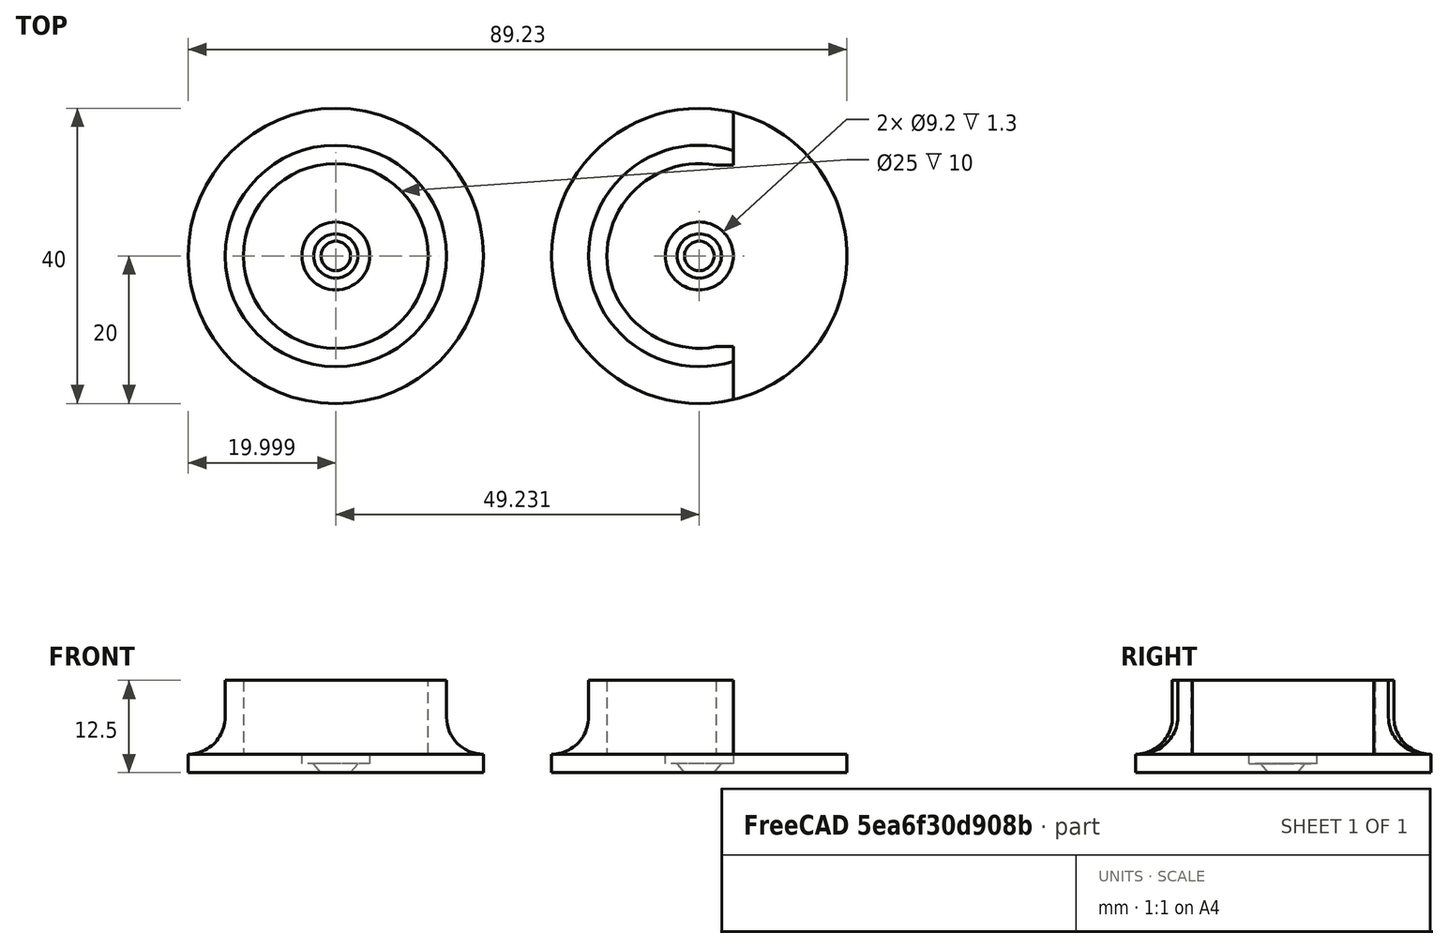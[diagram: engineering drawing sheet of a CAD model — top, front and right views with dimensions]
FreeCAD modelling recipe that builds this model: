
FCSTD DOCUMENT  (FreeCAD 0.20R29177 +233 (Git))
Label: FogasTarto
License: All rights reserved
LicenseURL: http://en.wikipedia.org/wiki/All_rights_reserved
objects: Part::Part2DObjectPython×10, Part::Cut×7, Part::Extrusion×5, Part::Cylinder×2, Part::MultiFuse×2, Part::Refine×2, Part::FeaturePython×1, Part::Torus×1, Part::Cone×1, Part::Feature×1
note: 32 computed .brp shape members not serialized (recipe doc carries the construction recipe); baked Part::Feature solids carry a one-line shape summary decoded from their .brp

FEATURE [Part::Cylinder] Cylinder
  Angle = 360
  AttacherType = Attacher::AttachEngine3D
  FirstAngle = 0
  Height = 10
  Radius = 12.5
  SecondAngle = 0
FEATURE [Part::Cylinder] Cylinder001
  Angle = 360
  AttacherType = Attacher::AttachEngine3D
  FirstAngle = 0
  Height = 10
  Radius = 15
  SecondAngle = 0
FEATURE [Part::Cut] Cut
  Base = -> Cylinder001
  Tool = -> Cylinder
FEATURE [Part::FeaturePython] Tube  # WARN: FeaturePython — macro-defined, semantics opaque (R4)
  AttacherType = Attacher::AttachEngine3D
  Height = 5
  InnerRadius = 15
  OuterRadius = 20
FEATURE [Part::Torus] Torus
  Angle1 = -180
  Angle2 = 180
  Angle3 = 360
  AttacherType = Attacher::AttachEngine3D
  Placement = pos=(0,-4.7e-15,5) rot=(0,0,1;0rad)
  Radius1 = 20
  Radius2 = 5
FEATURE [Part::Cut] Cut001
  Base = -> Tube
  Tool = -> Torus
FEATURE [Part::MultiFuse] Fusion
  Shapes = -> [Cut001,Cut]
FEATURE [Part::Part2DObjectPython] Circle  # Draft 2D object (typed FeaturePython)
  Area = 1256.64
  FirstAngle = 0
  LastAngle = 0
  MakeFace = true
  Placement = pos=(-7.1e-15,-3.7e-15,0) rot=(1,0,0;3.14159rad)
  Radius = 20
FEATURE [Part::Extrusion] Extrusion
  Base = -> Circle
  Dir = (0,0,-2.5)
  DirMode = 0
  FaceMakerClass = Part::FaceMakerBullseye
  LengthFwd = 0
  LengthRev = 0
  Solid = true
  Symmetric = false
FEATURE [Part::Part2DObjectPython] Circle001  # Draft 2D object (typed FeaturePython)
  Area = 12.5664
  FirstAngle = 0
  LastAngle = 0
  MakeFace = true
  Placement = pos=(-1.07e-14,-3e-15,-2.5) rot=(1,0,0;3.14159rad)
  Radius = 2
FEATURE [Part::Extrusion] Extrusion001
  Base = -> Circle001
  Dir = (0,0,42.0734)
  DirMode = 0
  FaceMakerClass = Part::FaceMakerBullseye
  LengthFwd = 0
  LengthRev = 0
  Solid = true
  Symmetric = false
FEATURE [Part::Cut] Cut002
  Base = -> Extrusion
  Tool = -> Extrusion001
FEATURE [Part::Part2DObjectPython] Circle002  # Draft 2D object (typed FeaturePython)
  Area = 66.4761
  FirstAngle = 0
  LastAngle = 0
  MakeFace = true
  Placement = pos=(-1.42e-14,-2.8e-15,0) rot=(0,0,1;0rad)
  Radius = 4.6
FEATURE [Part::Extrusion] Extrusion002
  Base = -> Circle002
  Dir = (0,0,-1.3)
  DirMode = 0
  FaceMakerClass = Part::FaceMakerBullseye
  LengthFwd = 0
  LengthRev = 0
  Solid = true
  Symmetric = false
FEATURE [Part::Cut] Cut003
  Base = -> Cut002
  Tool = -> Extrusion002
FEATURE [Part::Cone] Cone
  Angle = 360
  AttacherType = Attacher::AttachEngine3D
  Height = 1.2
  Placement = pos=(0,-3.1e-15,-2.5) rot=(0,0,1;0rad)
  Radius1 = 2
  Radius2 = 3
FEATURE [Part::Cut] Cut004
  Base = -> Cut003
  Tool = -> Cone
FEATURE [Part::MultiFuse] Fusion001
  Shapes = -> [Cut004,Fusion]
FEATURE [Part::Part2DObjectPython] Rectangle  # Draft 2D object (typed FeaturePython)
  Area = 3003.98
  ChamferSize = 0
  Columns = 1
  FilletRadius = 0
  Height = 50.7941
  Length = 59.1403
  MakeFace = true
  Placement = pos=(4.6,29.5702,3.6e-15) rot=(0.57735,-0.57735,-0.57735;2.0944rad)
  Rows = 1
FEATURE [Part::Part2DObjectPython] Line  # Draft 2D object (typed FeaturePython)
  Area = 0
  ChamferSize = 0
  Closed = false
  End = (4,29.5702,25.3971)
  FilletRadius = 0
  Length = 4
  MakeFace = true
  Placement = pos=(-1.42e-14,29.5702,25.3971) rot=(0,0,1;0rad)
  Points = (2) [(0,0,0),(4,0,0)]
  Start = (-1.42e-14,29.5702,25.3971)
  Subdivisions = 0
FEATURE [Part::Part2DObjectPython] Line001  # Draft 2D object (typed FeaturePython)
  Area = 0
  ChamferSize = 0
  Closed = false
  End = (4.6,-2.7e-15,0)
  FilletRadius = 0
  Length = 9.2
  MakeFace = true
  Placement = pos=(-4.6,-2.4e-15,0) rot=(0,0,1;0rad)
  Points = (2) [(0,0,0),(9.2,-5.63338e-16,0)]
  Start = (-4.6,-2.4e-15,0)
  Subdivisions = 0
FEATURE [Part::Refine] Fusion001001
  Placement = pos=(-49.2306,3e-15,0) rot=(0,0,1;0rad)
  Source = -> Fusion001
FEATURE [Part::Feature] Fusion001001001
  shape: bbox 54.12 x 54.12 x 12.5 mm, 10 faces (baked)
FEATURE [Part::Extrusion] Extrusion003
  Base = -> Rectangle
  Dir = (37.8377,0,0)
  DirMode = 0
  FaceMakerClass = Part::FaceMakerBullseye
  LengthFwd = 0
  LengthRev = 0
  Solid = true
  Symmetric = false
FEATURE [Part::Cut] Cut005
  Base = -> Fusion001001001
  Tool = -> Extrusion003
FEATURE [Part::Part2DObjectPython] Line002  # Draft 2D object (typed FeaturePython)
  Area = 0
  ChamferSize = 0
  Closed = false
  End = (0,24.1905,10)
  FilletRadius = 0
  Length = 48.381
  MakeFace = true
  Placement = pos=(0,-24.1905,10) rot=(0,0,1;0rad)
  Points = (2) [(0,0,0),(1.48124e-15,48.381,0)]
  Start = (0,-24.1905,10)
  Subdivisions = 0
FEATURE [Part::Part2DObjectPython] Line003  # Draft 2D object (typed FeaturePython)
  Area = 0
  ChamferSize = 0
  Closed = false
  End = (2.2636,-27.961,10)
  FilletRadius = 0
  Length = 51.9796
  MakeFace = true
  Placement = pos=(2.2636,24.0187,10) rot=(0,0,1;0rad)
  Points = (2) [(0,0,0),(-1.77636e-15,-51.9796,0)]
  Start = (2.2636,24.0187,10)
  Subdivisions = 0
FEATURE [Part::Part2DObjectPython] Line004  # Draft 2D object (typed FeaturePython)
  Area = 0
  ChamferSize = 0
  Closed = false
  End = (25.2332,12.2933,10)
  FilletRadius = 0
  Length = 22.9696
  MakeFace = true
  Placement = pos=(2.2636,12.2933,10) rot=(0,0,1;0rad)
  Points = (2) [(0,0,0),(22.9696,1.77636e-15,0)]
  Start = (2.2636,12.2933,10)
  Subdivisions = 0
FEATURE [Part::Part2DObjectPython] Rectangle001  # Draft 2D object (typed FeaturePython)
  Area = 564.747
  ChamferSize = 0
  Columns = 1
  FilletRadius = 0
  Height = 24.5867
  Length = 22.9696
  MakeFace = true
  Placement = pos=(2.2636,-12.2933,10) rot=(0,0,1;0rad)
  Rows = 1
FEATURE [Part::Extrusion] Extrusion004
  Base = -> Rectangle001
  Dir = (0,0,-10)
  DirMode = 0
  FaceMakerClass = Part::FaceMakerBullseye
  LengthFwd = 0
  LengthRev = 0
  Solid = true
  Symmetric = false
FEATURE [Part::Cut] Cut006
  Base = -> Cut005
  Tool = -> Extrusion004
FEATURE [Part::Refine] Cut006001
  Source = -> Cut006
